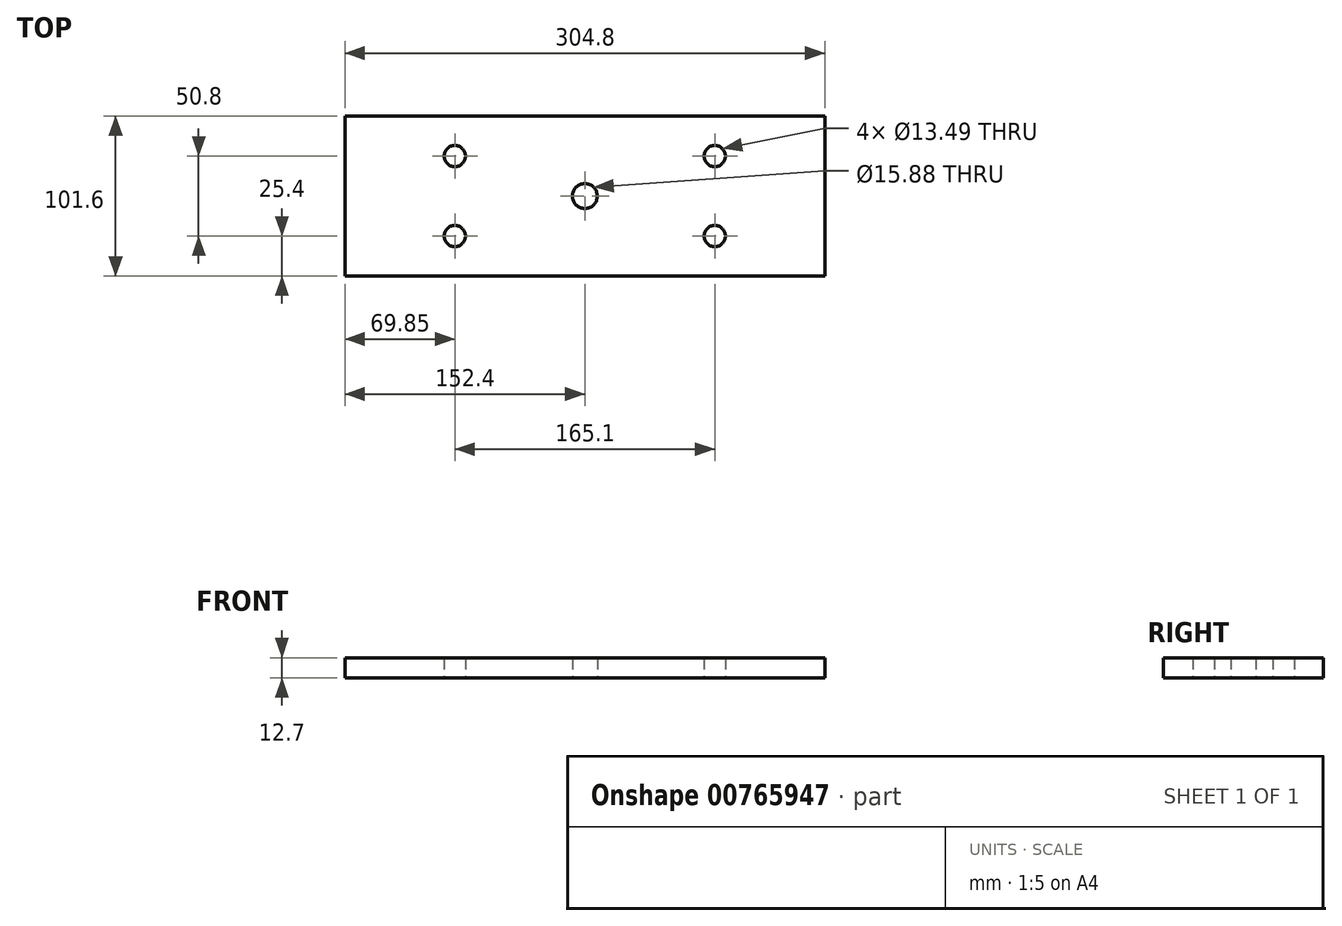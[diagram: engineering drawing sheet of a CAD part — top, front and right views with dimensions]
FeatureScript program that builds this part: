
annotation { "Feature Type Name" : "Feature", "Feature Type Description" : "" }
export const myFeature = defineFeature(function(context is Context, id is Id, definition is map)
    precondition{}
    {
        {
            var Q0;
            Q0=qCreatedBy(makeId("Top.planeOp"),FACE);
            var sketch = newSketch(context, id + "F0", { "sketchPlane" : qUnion([Q0])});
            skLineSegment(sketch, "E0.bottom", {"start": v(0, 101.6) * mm, "end": v(304.8, 101.6) * mm});
            skLineSegment(sketch, "E0.top", {"start": v(0, 0) * mm, "end": v(304.8, 0) * mm});
            skLineSegment(sketch, "E0.left", {"start": v(0, 101.6) * mm, "end": v(0, 0) * mm});
            skLineSegment(sketch, "E0.right", {"start": v(304.8, 101.6) * mm, "end": v(304.8, 0) * mm});
            skLineSegment(sketch, "E1", {"start": v(152.4, 101.6) * mm, "end": v(152.4, 0) * mm, "construction": true});
            skLineSegment(sketch, "E2", {"start": v(234.95, 101.6) * mm, "end": v(234.95, 0) * mm, "construction": true});
            skCircle(sketch, "E3", {"center": v(234.95, 76.2) * mm, "radius": 6.74 * mm});
            skCircle(sketch, "E4", {"center": v(234.95, 25.4) * mm, "radius": 6.74 * mm});
            skLineSegment(sketch, "E5.MirrorCS", {"start": v(69.85, 101.6) * mm, "end": v(69.85, 0) * mm, "construction": true});
            skCircle(sketch, "E6.MirrorC", {"center": v(69.85, 25.4) * mm, "radius": 6.74 * mm});
            skCircle(sketch, "E7.MirrorC", {"center": v(69.85, 76.2) * mm, "radius": 6.74 * mm});
            skSolve(sketch);
        }
        {
            var Q0;
            Q0 = qSketchRegion(id + "F0", true);
            extrude(context, id + "F1", {"entities" : qUnion([Q0]), "depth" : 12.7 * mm, "offsetDistance" : 25.4 * mm});
        }
        {
            var Q0;
            Q0=makeQuery(id+"F1.opExtrude","CAP_FACE",FACE,{"disambiguationData":[OSD([sQuery(id+"F0.wireOp",EDGE,"E0.bottom"),sQuery(id+"F0.wireOp",EDGE,"E0.top"),sQuery(id+"F0.wireOp",EDGE,"E0.left"),sQuery(id+"F0.wireOp",EDGE,"E0.right"),sQuery(id+"F0.wireOp",EDGE,"E3"),sQuery(id+"F0.wireOp",EDGE,"E4"),sQuery(id+"F0.wireOp",EDGE,"E6.MirrorC"),sQuery(id+"F0.wireOp",EDGE,"E7.MirrorC")])],"isStart":true});
            var sketch = newSketch(context, id + "F2", { "sketchPlane" : qUnion([Q0])});
            skCircle(sketch, "E8", {"center": v(152.4, -50.8) * mm, "radius": 7.94 * mm});
            skSolve(sketch);
        }
        {
            var Q0;
            Q0 = qSketchRegion(id + "F2", true);
            extrude(context, id + "F3", {"entities" : qUnion([Q0]), "operationType" : NewBodyOperationType.REMOVE, "oppositeDirection" : true, "depth" : 25.4 * mm, "offsetDistance" : 25.4 * mm});
        }
    });
